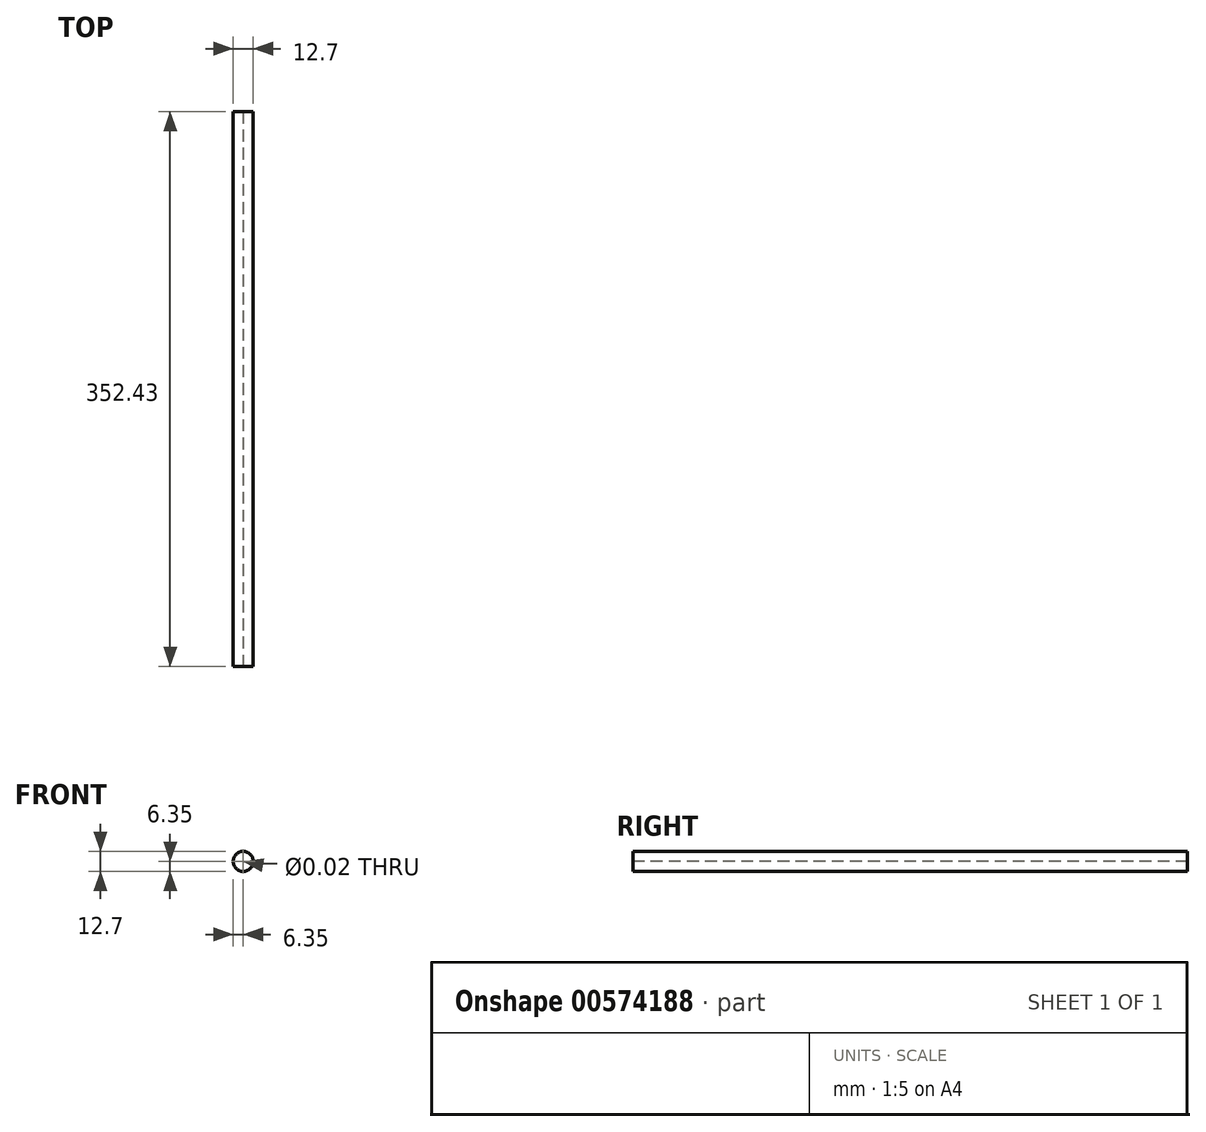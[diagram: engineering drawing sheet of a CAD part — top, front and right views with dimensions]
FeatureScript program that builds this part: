
annotation { "Feature Type Name" : "Feature", "Feature Type Description" : "" }
export const myFeature = defineFeature(function(context is Context, id is Id, definition is map)
    precondition{}
    {
        {
            var Q0;
            Q0=qCreatedBy(makeId("Front.planeOp"),FACE);
            var sketch = newSketch(context, id + "F0", { "sketchPlane" : qUnion([Q0])});
            skCircle(sketch, "E0", {"center": v(0, 0) * mm, "radius": 6.35 * mm});
            skLineSegment(sketch, "E1", {"start": v(-35.62, 0) * mm, "end": v(35.36, 0) * mm, "construction": true});
            skLineSegment(sketch, "E2", {"start": v(0, 0) * mm, "end": v(0, 31.87) * mm, "construction": true});
            skSolve(sketch);
        }
        {
            var Q0;
            Q0 = qSketchRegion(id + "F0", true);
            extrude(context, id + "F1", {"entities" : qUnion([Q0]), "oppositeDirection" : true, "depth" : 352.42 * mm, "offsetDistance" : 25.4 * mm});
        }
        {
            var Q0;
            Q0=makeQuery(id+"F1.opExtrude","CAP_FACE",FACE,{"disambiguationData":[OSD([sQuery(id+"F0.wireOp",EDGE,"E0")])],"isStart":true});
            cPlane(context, id + "F2", {"entities" : qUnion([Q0]), "cplaneType" : CPlaneType.OFFSET, "offset" : 25.4 * mm, "width" : 152.4 * mm, "height" : 152.4 * mm});
        }
        {
            var Q0;
            Q0=qCreatedBy(id+"F2.planeOp",FACE);
            var sketch = newSketch(context, id + "F3", { "sketchPlane" : qUnion([Q0])});
            skCircle(sketch, "E3", {"center": v(0, 0) * mm, "radius": 12.7 * mm, "construction": true});
            skSolve(sketch);
        }
        {
            var Q0;
            Q0=sQuery(id+"F3.wireOp",VERTEX,"E3.center");
            var Q1;
            Q1=makeQuery(id+"F1.opExtrude","SWEPT_BODY",BODY,{"disambiguationData":[OSD([sQuery(id+"F0.wireOp",EDGE,"E0")])]});
            hole(context, id + "F4", {"style" : HoleStyle.SIMPLE, "endStyle" : HoleEndStyle.THROUGH, "standardTappedOrClearance" : lookupTablePath({ "standard" : "ANSI", "size" : "7/16 (0.44)", "type" : "Drilled" }), "standardBlindInLast" : lookupTablePath({ "standard" : "ANSI", "size" : "7/16", "type" : "Drilled" }), "holeDiameter" : 7 / 406.4 * mm, "majorDiameter" : 6.35 * mm, "isTappedThrough" : true, "tappedDepth" : 12.7 * mm, "tapClearance" : 3, "locations" : qUnion([Q0]), "scope" : qUnion([Q1])});
        }
    });
